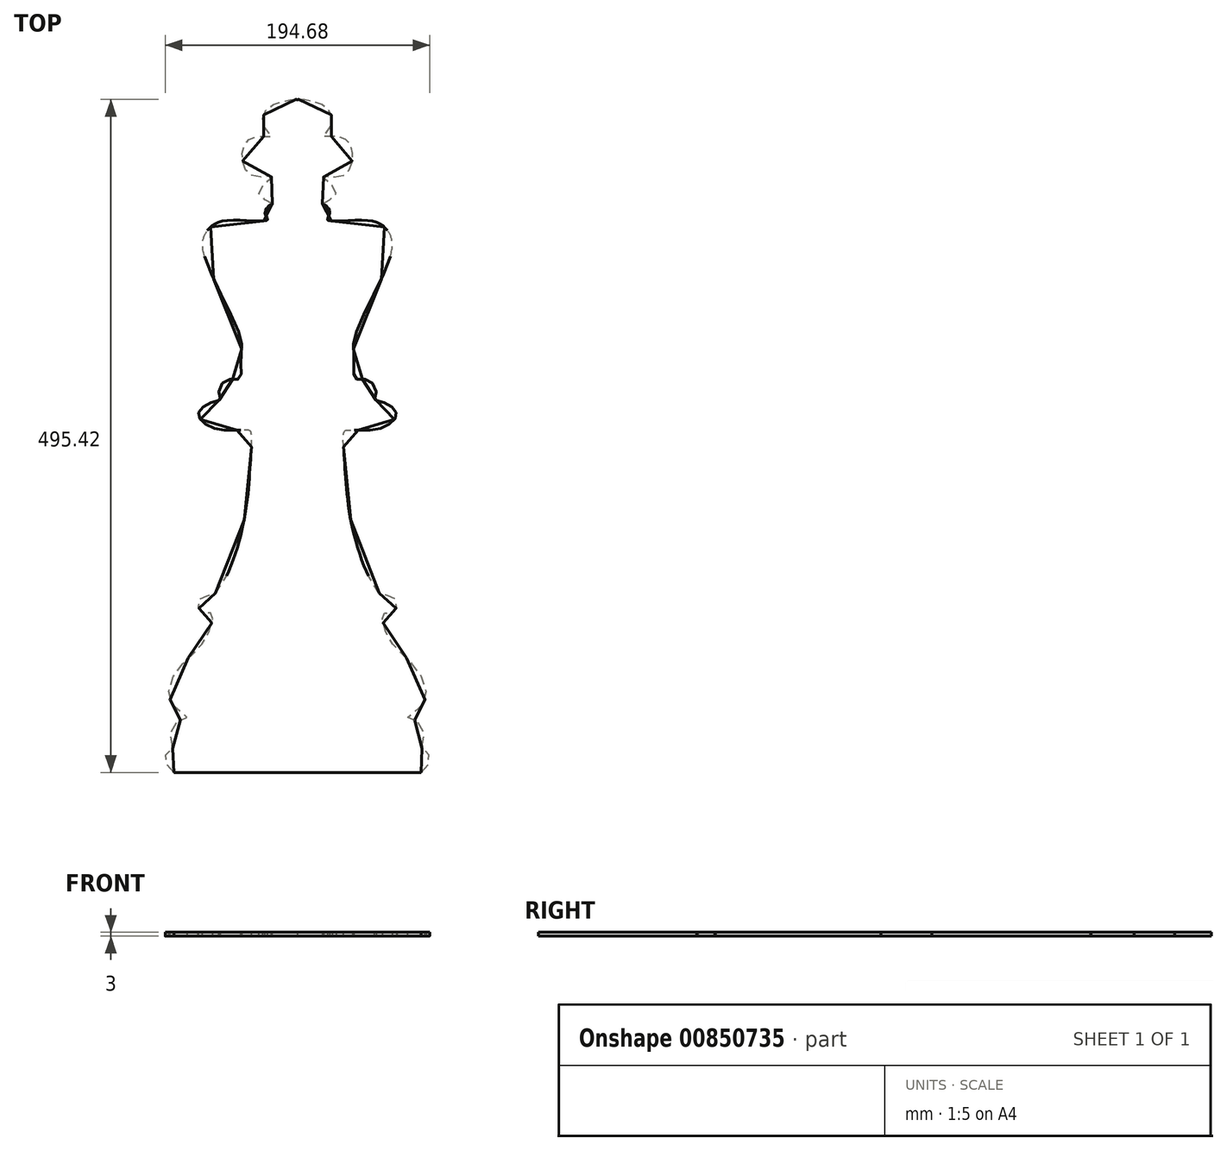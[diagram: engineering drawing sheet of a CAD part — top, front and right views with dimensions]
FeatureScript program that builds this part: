
annotation { "Feature Type Name" : "Feature", "Feature Type Description" : "" }
export const myFeature = defineFeature(function(context is Context, id is Id, definition is map)
    precondition{}
    {
        {
            var Q0;
            Q0=qCreatedBy(makeId("Top.planeOp"),FACE);
            var sketch = newSketch(context, id + "F0", { "sketchPlane" : qUnion([Q0])});
            skLineSegment(sketch, "E0", {"start": v(-250, 250) * mm, "end": v(250, -250) * mm, "construction": true});
            skLineSegment(sketch, "E1", {"start": v(250, 250) * mm, "end": v(-250, -250) * mm, "construction": true});
            skPoint(sketch, "E2", {"position": v(0, 0) * mm});
            skLineSegment(sketch, "E3", {"start": v(0, 250.01) * mm, "end": v(0, -249.99) * mm});
            skLineSegment(sketch, "E4", {"start": v(0, -249.99) * mm, "end": v(-90.99, -249.99) * mm});
            skFitSpline(sketch, "E5", {"points": [v(-90.99, -249.99) * mm, v(-97.06, -242.12) * mm, v(-94.96, -233.93) * mm, v(-90.99, -231.58) * mm, v(-93.32, -226.44) * mm, v(-88.87, -212.86) * mm, v(-80.91, -208.88) * mm, v(-87.93, -204.67) * mm, v(-94.72, -189.45) * mm, v(-84.26, -169.65) * mm, v(-71.55, -157.15) * mm, v(-63.36, -141.47) * mm, v(-63.12, -132.58) * mm, v(-67.34, -133.28) * mm, v(-72.02, -130.24) * mm, v(-72.78, -124.14) * mm, v(-68.58, -119.94) * mm, v(-62.19, -119.47) * mm, v(-41.12, -72.9) * mm, v(-34.34, -16.58) * mm, v(-34.84, 1.46) * mm, v(-38.64, 2.12) * mm, v(-44.77, 2.12) * mm, v(-59.14, 2.94) * mm, v(-71.55, 9.97) * mm, v(-72.25, 16.05) * mm, v(-62.8, 22.6) * mm, v(-56.57, 24.95) * mm, v(-57.84, 27.57) * mm, v(-52.7, 39) * mm, v(-42.76, 39.92) * mm, v(-41.62, 53.72) * mm, v(-42.28, 71.1) * mm, v(-69.2, 133.32) * mm, v(-65.7, 149.7) * mm, v(-51.65, 156.49) * mm, v(-22.16, 156.72) * mm, v(-23.67, 161.1) * mm, v(-21.06, 167.04) * mm, v(-18.42, 168.66) * mm, v(-28.5, 176.52) * mm, v(-19.12, 188.32) * mm, v(-31.3, 188.79) * mm, v(-39.72, 197.45) * mm, v(-39.02, 212.2) * mm, v(-29.42, 218.28) * mm, v(-18.89, 218.28) * mm, v(-23.8, 224.13) * mm, v(-23.1, 237.7) * mm, v(-8.12, 244.73) * mm, v(0, 245.38) * mm], "startDerivative": vector(-423.63, 380.08) * mm, "endDerivative": vector(422.75, -24.47) * mm});
            skFitSpline(sketch, "E6.MirrorCS", {"points": [v(90.99, -249.99) * mm, v(97.06, -242.12) * mm, v(94.96, -233.93) * mm, v(90.99, -231.58) * mm, v(93.32, -226.44) * mm, v(88.87, -212.86) * mm, v(80.91, -208.88) * mm, v(87.93, -204.67) * mm, v(94.72, -189.45) * mm, v(84.26, -169.65) * mm, v(71.55, -157.15) * mm, v(63.36, -141.47) * mm, v(63.12, -132.58) * mm, v(67.34, -133.28) * mm, v(72.02, -130.24) * mm, v(72.78, -124.14) * mm, v(68.58, -119.94) * mm, v(62.19, -119.47) * mm, v(41.12, -72.9) * mm, v(34.34, -16.58) * mm, v(34.84, 1.46) * mm, v(38.64, 2.12) * mm, v(44.77, 2.12) * mm, v(59.14, 2.94) * mm, v(71.55, 9.97) * mm, v(72.25, 16.05) * mm, v(62.8, 22.6) * mm, v(56.57, 24.95) * mm, v(57.84, 27.57) * mm, v(52.7, 39) * mm, v(42.76, 39.92) * mm, v(41.62, 53.72) * mm, v(42.28, 71.1) * mm, v(69.2, 133.32) * mm, v(65.7, 149.7) * mm, v(51.65, 156.49) * mm, v(22.16, 156.72) * mm, v(23.67, 161.1) * mm, v(21.06, 167.04) * mm, v(18.42, 168.66) * mm, v(28.5, 176.52) * mm, v(19.12, 188.32) * mm, v(31.3, 188.79) * mm, v(39.72, 197.45) * mm, v(39.02, 212.2) * mm, v(29.42, 218.28) * mm, v(18.89, 218.28) * mm, v(23.8, 224.13) * mm, v(23.1, 237.7) * mm, v(8.12, 244.73) * mm, v(0, 245.38) * mm], "startDerivative": vector(423.63, 380.08) * mm, "endDerivative": vector(-422.75, -24.47) * mm});
            skLineSegment(sketch, "E7.MirrorCS", {"start": v(0, -249.99) * mm, "end": v(90.99, -249.99) * mm});
            skLineSegment(sketch, "E8.bottom", {"start": v(-1, 249.99) * mm, "end": v(1, 249.99) * mm});
            skLineSegment(sketch, "E8.top", {"start": v(-1, -249.99) * mm, "end": v(1, -249.99) * mm});
            skLineSegment(sketch, "E8.left", {"start": v(-1, 249.99) * mm, "end": v(-1, -249.99) * mm});
            skLineSegment(sketch, "E8.right", {"start": v(1, 249.99) * mm, "end": v(1, -249.99) * mm});
            skLineSegment(sketch, "E9", {"start": v(-1, 0) * mm, "end": v(1, 0) * mm});
            skSolve(sketch);
        }
        {
            var Q0;
            {var subQ0=sQuery(id+"F0.wireOp",EDGE,"E7.MirrorCS");Q0=makeQuery(id+"F0.imprint","IMPRINT",FACE,{"disambiguationData":[TD([[makeQuery(id+"F0.imprint","IMPRINT",EDGE,{"derivedFrom":subQ0}),1.0]])]});}
            var Q1;
            {var subQ0=sQuery(id+"F0.wireOp",EDGE,"E4");Q1=makeQuery(id+"F0.imprint","IMPRINT",FACE,{"disambiguationData":[TD([[makeQuery(id+"F0.imprint","IMPRINT",EDGE,{"derivedFrom":subQ0}),-1.0]])]});}
            var Q2;
            {var subQ0=sQuery(id+"F0.wireOp",EDGE,"E8.top");var subQ1=sQuery(id+"F0.wireOp",EDGE,"E3");var subQ2=makeQuery(id+"F0.imprint","INTERSECT",VERTEX,{"derivedFrom":[subQ1,subQ0]});Q2=makeQuery(id+"F0.imprint","IMPRINT",FACE,{"disambiguationData":[TD([[makeQuery(id+"F0.imprint","IMPRINT",EDGE,{"disambiguationData":[TD([[subQ2,1.0]])],"derivedFrom":subQ1}),-1.0]])]});}
            var Q3;
            {var subQ0=sQuery(id+"F0.wireOp",EDGE,"E8.top");var subQ1=sQuery(id+"F0.wireOp",EDGE,"E3");var subQ2=makeQuery(id+"F0.imprint","INTERSECT",VERTEX,{"derivedFrom":[subQ1,subQ0]});Q3=makeQuery(id+"F0.imprint","IMPRINT",FACE,{"disambiguationData":[TD([[makeQuery(id+"F0.imprint","IMPRINT",EDGE,{"disambiguationData":[TD([[subQ2,1.0]])],"derivedFrom":subQ1}),1.0]])]});}
            extrude(context, id + "F1", {"entities" : qUnion([Q0, Q1, Q2, Q3]), "depth" : 3 * mm, "offsetDistance" : 25 * mm});
        }
    });
